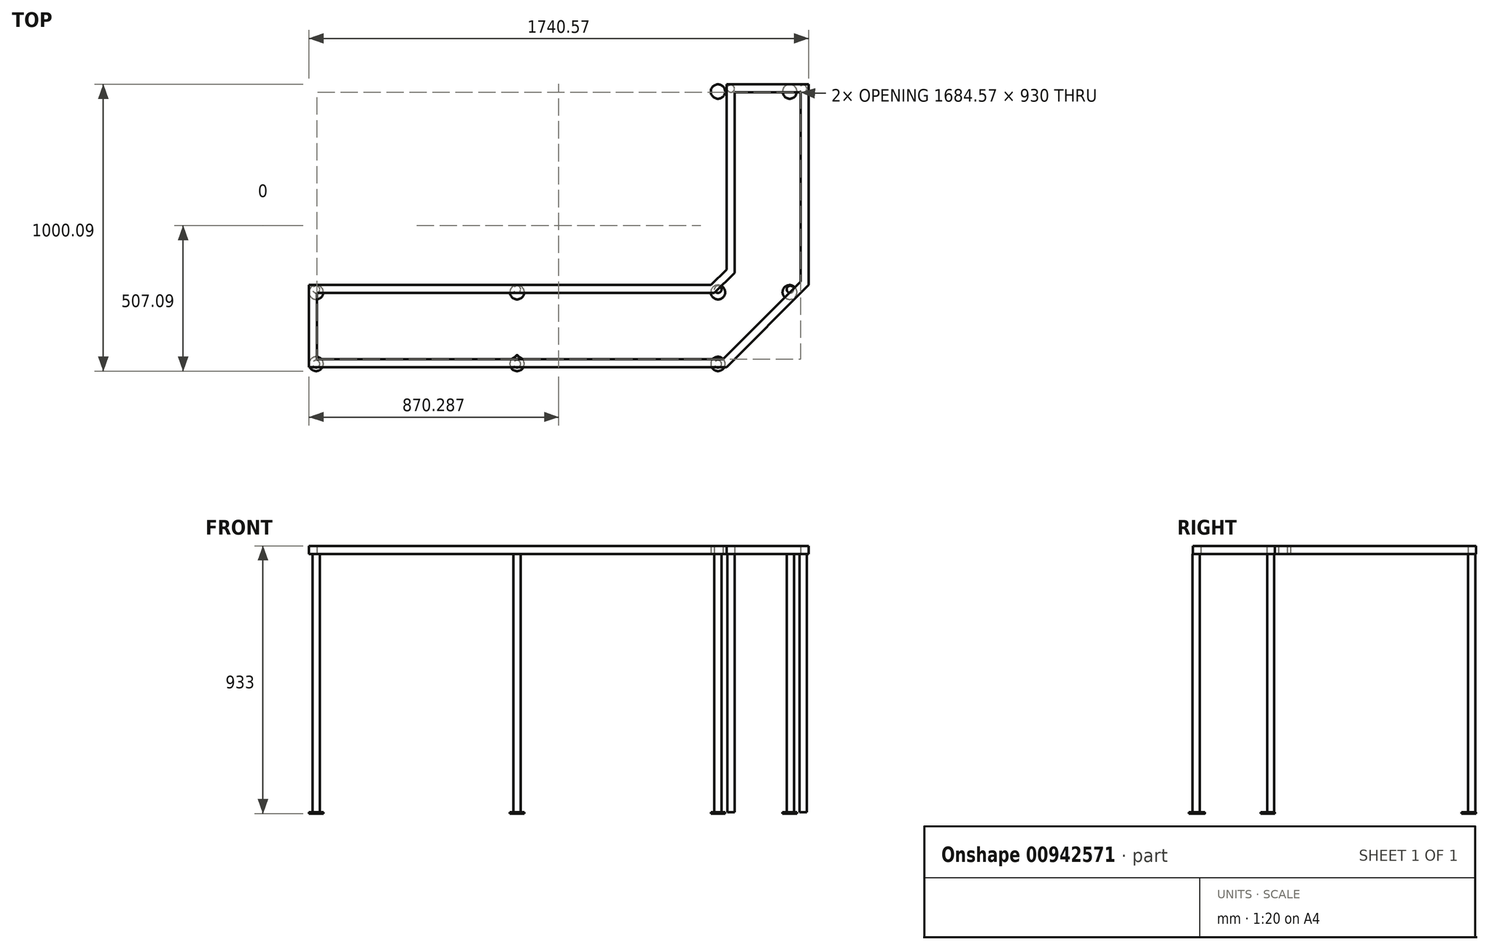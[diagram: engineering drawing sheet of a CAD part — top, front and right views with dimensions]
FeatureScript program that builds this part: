
annotation { "Feature Type Name" : "Feature", "Feature Type Description" : "" }
export const myFeature = defineFeature(function(context is Context, id is Id, definition is map)
    precondition{}
    {
        {
            var Q0;
            Q0=qCreatedBy(makeId("Top.planeOp"),FACE);
            var sketch = newSketch(context, id + "F0", { "sketchPlane" : qUnion([Q0])});
            skCircle(sketch, "E0", {"center": v(0, 0) * mm, "radius": 25 * mm});
            skCircle(sketch, "E1", {"center": v(0, 250) * mm, "radius": 25 * mm});
            skCircle(sketch, "E2", {"center": v(700, 0) * mm, "radius": 25 * mm});
            skCircle(sketch, "E3", {"center": v(700, 250) * mm, "radius": 25 * mm});
            skCircle(sketch, "E4", {"center": v(1400, 0) * mm, "radius": 25 * mm});
            skLineSegment(sketch, "E5", {"start": v(-139.53, 250) * mm, "end": v(2082.75, 250) * mm, "construction": true});
            skLineSegment(sketch, "E6", {"start": v(-155.28, 0) * mm, "end": v(2150.3, 0) * mm, "construction": true});
            skCircle(sketch, "E7", {"center": v(1400, 250) * mm, "radius": 25 * mm});
            skLineSegment(sketch, "E8", {"start": v(1400, -1165.16) * mm, "end": v(1400, 3065.16) * mm, "construction": true});
            skLineSegment(sketch, "E9", {"start": v(1400, 0) * mm, "end": v(2621.83, 1221.83) * mm, "construction": true});
            skLineSegment(sketch, "E10", {"start": v(1650, 250) * mm, "end": v(1650, 3237.7) * mm, "construction": true});
            skCircle(sketch, "E11", {"center": v(1650, 250) * mm, "radius": 25 * mm});
            skCircle(sketch, "E12", {"center": v(1650, 950) * mm, "radius": 25 * mm});
            skCircle(sketch, "E13", {"center": v(1400, 950) * mm, "radius": 25 * mm});
            skLineSegment(sketch, "E14", {"start": v(-139.53, 250) * mm, "end": v(-155.28, 0) * mm, "construction": true});
            skLineSegment(sketch, "E15", {"start": v(-241.15, 125) * mm, "end": v(2480.34, 125) * mm, "construction": true});
            skPoint(sketch, "E15.startSnap0", {"position": v(-147.4, 125) * mm});
            skLineSegment(sketch, "E16", {"start": v(350, 500) * mm, "end": v(350, -439.43) * mm, "construction": true});
            skLineSegment(sketch, "E17", {"start": v(700, 250) * mm, "end": v(1400, 250) * mm, "construction": true});
            skCircle(sketch, "E18.MirrorC", {"center": v(700, 27) * mm, "radius": 4 * mm});
            skLineSegment(sketch, "E19", {"start": v(1375.34, 950) * mm, "end": v(1819.23, 950) * mm, "construction": true});
            skSolve(sketch);
        }
        {
            var Q0;
            Q0 = qSketchRegion(id + "F0", true);
            extrude(context, id + "F1", {"entities" : qUnion([Q0]), "depth" : 5 * mm, "offsetDistance" : 25 * mm});
        }
        {
            var Q0;
            Q0=makeQuery(id+"F1.opExtrude","CAP_FACE",FACE,{"disambiguationData":[OSD([sQuery(id+"F0.wireOp",EDGE,"E0")])],"isStart":false});
            var sketch = newSketch(context, id + "F2", { "sketchPlane" : qUnion([Q0])});
            skCircle(sketch, "E20", {"center": v(0, 0) * mm, "radius": 12.5 * mm});
            skLineSegment(sketch, "E21", {"start": v(-416.87, 0) * mm, "end": v(2366.19, 0) * mm, "construction": true});
            skLineSegment(sketch, "E22.0", {"start": v(-416.87, 260) * mm, "end": v(2366.19, 260) * mm, "construction": true});
            skLineSegment(sketch, "E23.0", {"start": v(700, -194.36) * mm, "end": v(700, 924.07) * mm, "construction": true});
            skLineSegment(sketch, "E24.0", {"start": v(1400, -194.36) * mm, "end": v(1400, 2539.46) * mm, "construction": true});
            skLineSegment(sketch, "E25.0", {"start": v(1652, -194.36) * mm, "end": v(1652, 2539.46) * mm, "construction": true});
            skCircle(sketch, "E26", {"center": v(0, 260) * mm, "radius": 12.5 * mm});
            skCircle(sketch, "E27", {"center": v(700, 260) * mm, "radius": 12.5 * mm});
            skCircle(sketch, "E28", {"center": v(1400, 260) * mm, "radius": 12.5 * mm});
            skCircle(sketch, "E29", {"center": v(1400, 0) * mm, "radius": 12.5 * mm});
            skCircle(sketch, "E30", {"center": v(700, 0) * mm, "radius": 12.5 * mm});
            skCircle(sketch, "E31", {"center": v(1652, 260) * mm, "radius": 12.5 * mm});
            skLineSegment(sketch, "E32.0", {"start": v(-416.87, 960) * mm, "end": v(2366.19, 960) * mm, "construction": true});
            skCircle(sketch, "E33", {"center": v(1445, 960) * mm, "radius": 12.5 * mm});
            skCircle(sketch, "E34", {"center": v(1697, 960) * mm, "radius": 12.5 * mm});
            skLineSegment(sketch, "E35", {"start": v(0, 0) * mm, "end": v(0, 260) * mm, "construction": true});
            skSolve(sketch);
        }
        {
            var Q0;
            Q0 = qSketchRegion(id + "F2", true);
            extrude(context, id + "F3", {"entities" : qUnion([Q0]), "operationType" : NewBodyOperationType.ADD, "depth" : 900 * mm, "offsetDistance" : 25 * mm});
        }
        {
            var Q0;
            Q0 = qSketchRegion(id + "F2", true);
            extrude(context, id + "F4", {"entities" : qUnion([Q0]), "depth" : 900 * mm, "offsetDistance" : 25 * mm});
        }
        {
            var Q0;
            Q0=makeQuery(id+"F3.opExtrude","CAP_FACE",FACE,{"disambiguationData":[OSD([sQuery(id+"F2.wireOp",EDGE,"E20")])],"isStart":false});
            var sketch = newSketch(context, id + "F5", { "sketchPlane" : qUnion([Q0])});
            skLineSegment(sketch, "E36.bottom", {"start": v(-25, -10.9) * mm, "end": v(1429.57, -10.9) * mm});
            skLineSegment(sketch, "E36.top", {"start": v(-25, 275.1) * mm, "end": v(1375, 275.1) * mm});
            skLineSegment(sketch, "E36.left", {"start": v(-25, -10.9) * mm, "end": v(-25, 275.1) * mm});
            skLineSegment(sketch, "E37.top", {"start": v(1429.57, 975.1) * mm, "end": v(1715.57, 975.1) * mm});
            skLineSegment(sketch, "E37.left", {"start": v(1429.57, 329.5) * mm, "end": v(1429.57, 975.1) * mm});
            skLineSegment(sketch, "E38", {"start": v(1429.57, -10.9) * mm, "end": v(1715.57, 275.1) * mm});
            skLineSegment(sketch, "E39.trimOffspring", {"start": v(1715.57, 275.1) * mm, "end": v(1715.57, 975.1) * mm});
            skLineSegment(sketch, "E40", {"start": v(0, 0) * mm, "end": v(0, -10.9) * mm, "construction": true});
            skLineSegment(sketch, "E41", {"start": v(0, 0) * mm, "end": v(-25, 0) * mm, "construction": true});
            skLineSegment(sketch, "E42", {"start": v(0, 0) * mm, "end": v(0, 250.1) * mm, "construction": true});
            skLineSegment(sketch, "E43", {"start": v(-80.8, 250.1) * mm, "end": v(2310.18, 250.1) * mm, "construction": true});
            skLineSegment(sketch, "E44.0", {"start": v(3, 247.1) * mm, "end": v(1386.57, 247.1) * mm});
            skLineSegment(sketch, "E44.1", {"start": v(3, 17.1) * mm, "end": v(3, 247.1) * mm});
            skLineSegment(sketch, "E44.2", {"start": v(3, 17.1) * mm, "end": v(1417.98, 17.1) * mm});
            skLineSegment(sketch, "E45.0", {"start": v(1457.57, 317.89) * mm, "end": v(1457.57, 947.1) * mm});
            skLineSegment(sketch, "E45.1", {"start": v(1457.57, 947.1) * mm, "end": v(1687.57, 947.1) * mm});
            skLineSegment(sketch, "E45.2", {"start": v(1687.57, 286.69) * mm, "end": v(1687.57, 947.1) * mm});
            skLineSegment(sketch, "E45.3", {"start": v(1417.98, 17.1) * mm, "end": v(1687.57, 286.69) * mm});
            skLineSegment(sketch, "E46", {"start": v(1386.57, 247.1) * mm, "end": v(1457.57, 317.89) * mm});
            skPoint(sketch, "E47", {"position": v(1417.98, 17.1) * mm});
            skLineSegment(sketch, "E48.0", {"start": v(1375, 275.1) * mm, "end": v(1429.57, 329.5) * mm});
            skPoint(sketch, "E49", {"position": v(1375, 275.1) * mm});
            skPoint(sketch, "E50", {"position": v(1429.57, 329.5) * mm});
            skSolve(sketch);
        }
        {
            var Q0;
            Q0 = qSketchRegion(id + "F5", true);
            extrude(context, id + "F6", {"entities" : qUnion([Q0]), "depth" : 28 * mm, "offsetDistance" : 25 * mm});
        }
        {
            var Q0;
            Q0 = qSketchRegion(id + "F5", true);
            extrude(context, id + "F7", {"entities" : qUnion([Q0]), "depth" : 28 * mm, "offsetDistance" : 25 * mm});
        }
    });
